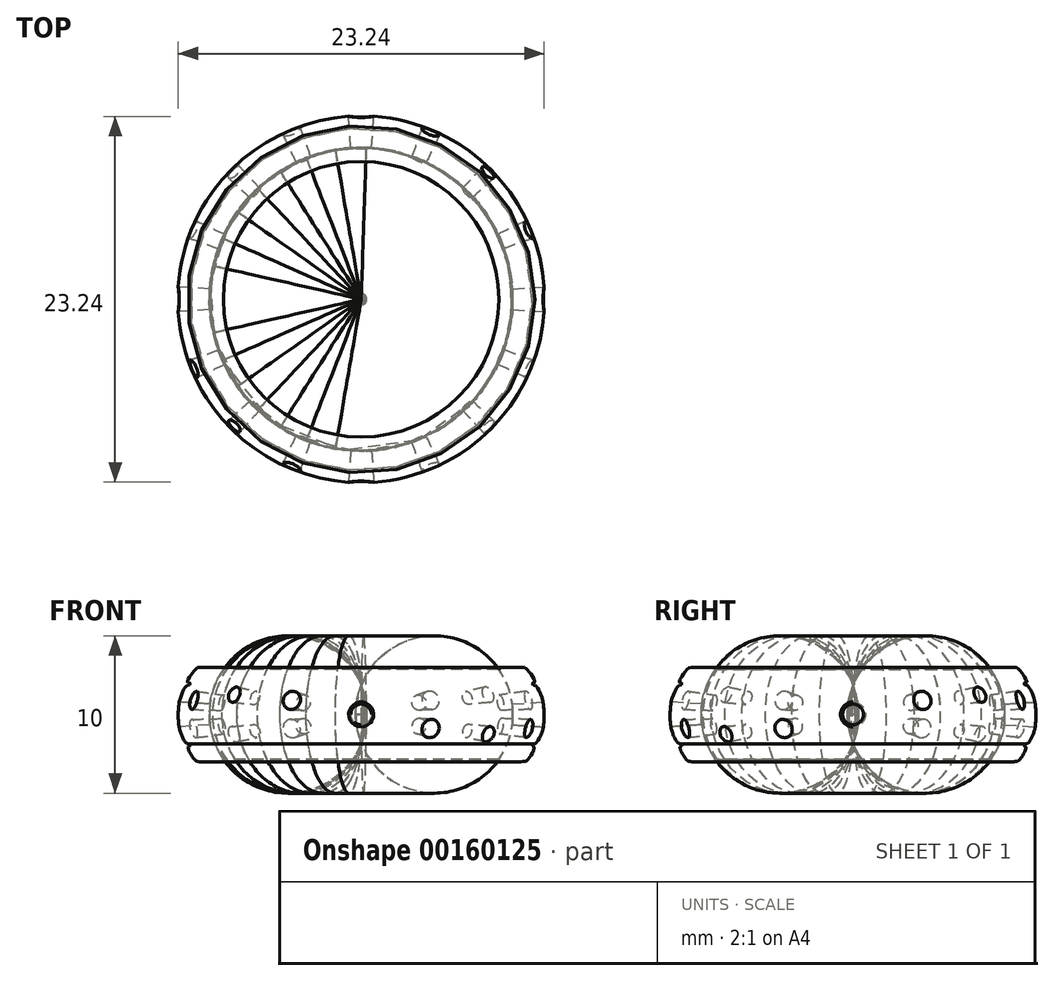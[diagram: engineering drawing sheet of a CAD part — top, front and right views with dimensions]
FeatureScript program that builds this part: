
annotation { "Feature Type Name" : "Feature", "Feature Type Description" : "" }
export const myFeature = defineFeature(function(context is Context, id is Id, definition is map)
    precondition{}
    {
        {
            var Q0;
            Q0=qCreatedBy(makeId("Top.planeOp"),FACE);
            var sketch = newSketch(context, id + "F0", { "sketchPlane" : qUnion([Q0])});
            skCircle(sketch, "E0", {"center": v(0, 0) * mm, "radius": 9.65 * mm});
            skLineSegment(sketch, "E1", {"start": v(-9.65, 0) * mm, "end": v(9.65, 0) * mm, "construction": true});
            skLineSegment(sketch, "E2", {"start": v(0, 9.65) * mm, "end": v(0, -9.65) * mm, "construction": true});
            skCircle(sketch, "E3", {"center": v(0, 0) * mm, "radius": 13.5 * mm});
            skSolve(sketch);
        }
        {
            var Q0;
            Q0=qCreatedBy(makeId("Top.planeOp"),FACE);
            var sketch = newSketch(context, id + "F1", { "sketchPlane" : qUnion([Q0])});
            skCircle(sketch, "E4.0", {"center": v(0, 0) * mm, "radius": 13.5 * mm, "construction": true});
            skLineSegment(sketch, "E5", {"start": v(0, 0) * mm, "end": v(-13.5, 0) * mm, "construction": true});
            skLineSegment(sketch, "E6", {"start": v(-13.5, 4.4) * mm, "end": v(-13.5, -4.4) * mm, "construction": true});
            skLineSegment(sketch, "E7.1.0", {"start": v(0, 0) * mm, "end": v(0, -13.5) * mm, "construction": true});
            skLineSegment(sketch, "E7.1.1", {"start": v(-4.4, -13.5) * mm, "end": v(4.4, -13.5) * mm, "construction": true});
            skLineSegment(sketch, "E7.2.0", {"start": v(0, 0) * mm, "end": v(13.5, 0) * mm, "construction": true});
            skLineSegment(sketch, "E7.2.1", {"start": v(13.5, -4.4) * mm, "end": v(13.5, 4.4) * mm, "construction": true});
            skLineSegment(sketch, "E7.3.0", {"start": v(0, 0) * mm, "end": v(0, 13.5) * mm, "construction": true});
            skLineSegment(sketch, "E7.3.1", {"start": v(4.4, 13.5) * mm, "end": v(-4.4, 13.5) * mm, "construction": true});
            skSolve(sketch);
        }
        {
            var Q0;
            Q0=qCreatedBy(makeId("Top.planeOp"),FACE);
            var sketch = newSketch(context, id + "F2", { "sketchPlane" : qUnion([Q0])});
            skCircle(sketch, "E8.0", {"center": v(0, 0) * mm, "radius": 13.5 * mm});
            skLineSegment(sketch, "E9", {"start": v(0, 0) * mm, "end": v(9.55, -9.55) * mm, "construction": true});
            skLineSegment(sketch, "E10", {"start": v(12.38, -6.71) * mm, "end": v(6.71, -12.38) * mm, "construction": true});
            skLineSegment(sketch, "E11.1.0", {"start": v(6.71, 12.38) * mm, "end": v(12.38, 6.71) * mm, "construction": true});
            skLineSegment(sketch, "E11.1.1", {"start": v(0, 0) * mm, "end": v(9.55, 9.55) * mm, "construction": true});
            skLineSegment(sketch, "E11.2.0", {"start": v(-12.38, 6.71) * mm, "end": v(-6.71, 12.38) * mm, "construction": true});
            skLineSegment(sketch, "E11.2.1", {"start": v(0, 0) * mm, "end": v(-9.55, 9.55) * mm, "construction": true});
            skLineSegment(sketch, "E11.3.0", {"start": v(-6.71, -12.38) * mm, "end": v(-12.38, -6.71) * mm, "construction": true});
            skLineSegment(sketch, "E11.3.1", {"start": v(0, 0) * mm, "end": v(-9.55, -9.55) * mm, "construction": true});
            skSolve(sketch);
        }
        {
            var Q0;
            Q0=qCreatedBy(makeId("Top.planeOp"),FACE);
            var sketch = newSketch(context, id + "F3", { "sketchPlane" : qUnion([Q0])});
            skCircle(sketch, "E12.0", {"center": v(0, 0) * mm, "radius": 13.5 * mm});
            skLineSegment(sketch, "E13", {"start": v(0, 0) * mm, "end": v(5.17, -12.47) * mm, "construction": true});
            skLineSegment(sketch, "E14", {"start": v(3.59, -13.13) * mm, "end": v(6.75, -11.82) * mm, "construction": true});
            skLineSegment(sketch, "E15.1.0", {"start": v(0, 0) * mm, "end": v(12.47, -5.17) * mm, "construction": true});
            skLineSegment(sketch, "E15.1.1", {"start": v(11.82, -6.75) * mm, "end": v(13.13, -3.59) * mm, "construction": true});
            skLineSegment(sketch, "E15.2.0", {"start": v(0, 0) * mm, "end": v(12.47, 5.17) * mm, "construction": true});
            skLineSegment(sketch, "E15.2.1", {"start": v(13.13, 3.59) * mm, "end": v(11.82, 6.75) * mm, "construction": true});
            skLineSegment(sketch, "E15.3.0", {"start": v(0, 0) * mm, "end": v(5.17, 12.47) * mm, "construction": true});
            skLineSegment(sketch, "E15.3.1", {"start": v(6.75, 11.82) * mm, "end": v(3.59, 13.13) * mm, "construction": true});
            skLineSegment(sketch, "E16.3.4.0", {"start": v(-3.59, 13.13) * mm, "end": v(-6.75, 11.82) * mm, "construction": true});
            skLineSegment(sketch, "E16.4.4.0", {"start": v(0, 0) * mm, "end": v(-5.17, 12.47) * mm, "construction": true});
            skLineSegment(sketch, "E16.3.5.0", {"start": v(-11.82, 6.75) * mm, "end": v(-13.13, 3.59) * mm, "construction": true});
            skLineSegment(sketch, "E16.4.5.0", {"start": v(0, 0) * mm, "end": v(-12.47, 5.17) * mm, "construction": true});
            skLineSegment(sketch, "E16.3.6.0", {"start": v(-13.13, -3.59) * mm, "end": v(-11.82, -6.75) * mm, "construction": true});
            skLineSegment(sketch, "E16.4.6.0", {"start": v(0, 0) * mm, "end": v(-12.47, -5.17) * mm, "construction": true});
            skLineSegment(sketch, "E16.3.7.0", {"start": v(-6.75, -11.82) * mm, "end": v(-3.59, -13.13) * mm, "construction": true});
            skLineSegment(sketch, "E16.4.7.0", {"start": v(0, 0) * mm, "end": v(-5.17, -12.47) * mm, "construction": true});
            skSolve(sketch);
        }
        {
            var Q0;
            Q0=qCreatedBy(makeId("Front.planeOp"),FACE);
            var sketch = newSketch(context, id + "F4", { "sketchPlane" : qUnion([Q0])});
            skLineSegment(sketch, "E17.0", {"start": v(-9.65, 0) * mm, "end": v(9.65, 0) * mm});
            skLineSegment(sketch, "E18", {"start": v(-9.65, 0) * mm, "end": v(-17.86, 0) * mm, "construction": true});
            skPoint(sketch, "E19", {"position": v(-9.87, 0) * mm});
            skCircle(sketch, "E20", {"center": v(-4.65, 0) * mm, "radius": 5 * mm});
            skFitSpline(sketch, "E21", {"points": [v(-9.87, 3) * mm, v(-10.53, 2.87) * mm, v(-11.03, 2.12) * mm, v(-11.01, 2.04) * mm, v(-10.9, 2.02) * mm, v(-10.9, 1.88) * mm, v(-11.05, 1.85) * mm, v(-11.65, 0) * mm, v(-11.07, -1.84) * mm, v(-10.9, -1.87) * mm, v(-10.88, -2) * mm, v(-10.99, -2.07) * mm, v(-10.61, -2.83) * mm, v(-9.87, -3) * mm], "startDerivative": vector(-13.36, 0) * mm, "endDerivative": vector(14.23, 0) * mm});
            skLineSegment(sketch, "E22", {"start": v(-9.87, 3) * mm, "end": v(-9.05, 3) * mm});
            skLineSegment(sketch, "E23", {"start": v(-8.65, 2.6) * mm, "end": v(-8.65, -2.6) * mm});
            skLineSegment(sketch, "E24", {"start": v(-9.05, -3) * mm, "end": v(-9.87, -3) * mm});
            skPoint(sketch, "E25.visualSharp", {"position": v(-8.65, 3) * mm});
            skArc(sketch, "E25.filletArc", {"start": v(-8.65, 2.6) * mm, "mid": v(-8.77, 2.88) * mm, "end": v(-9.05, 3) * mm});
            skPoint(sketch, "E26.visualSharp", {"position": v(-8.65, -3) * mm});
            skArc(sketch, "E26.filletArc", {"start": v(-9.05, -3) * mm, "mid": v(-8.77, -2.88) * mm, "end": v(-8.65, -2.6) * mm});
            skLineSegment(sketch, "E27", {"start": v(0, 17.35) * mm, "end": v(0, -28.4) * mm, "construction": true});
            skSolve(sketch);
        }
        {
            var Q0;
            Q0=sQuery(id+"F1.wireOp",EDGE,"E6");
            cPlane(context, id + "F5", {"entities" : qUnion([Q0]), "cplaneType" : CPlaneType.LINE_ANGLE, "offset" : 25 * mm, "angle" : 90 * degree, "width" : 150 * mm, "height" : 150 * mm});
        }
        {
            var Q0;
            Q0=qCreatedBy(id+"F5.planeOp",FACE);
            var sketch = newSketch(context, id + "F6", { "sketchPlane" : qUnion([Q0])});
            skLineSegment(sketch, "E28", {"start": v(0, 2.8) * mm, "end": v(0, -2.73) * mm, "construction": true});
            skCircle(sketch, "E29", {"center": v(0, 0) * mm, "radius": 0.93 * mm});
            skSolve(sketch);
        }
        {
            var Q0;
            Q0=makeQuery(id+"F4.imprint","IMPRINT",FACE,{"disambiguationData":[TD([[makeQuery(id+"F4.imprint","IMPRINT",EDGE,{"derivedFrom":sQuery(id+"F4.wireOp",EDGE,"E21")}),1.0]])]});
            var Q1;
            Q1=sQuery(id+"F4.wireOp",EDGE,"E27");
            revolve(context, id + "F7", {"entities" : qUnion([Q0]), "axis" : qUnion([Q1]), "revolveType" : RevolveType.FULL});
        }
        {
            var Q0;
            Q0=makeQuery(id+"F6.imprint","IMPRINT",FACE,{"disambiguationData":[TD([[makeQuery(id+"F6.imprint","IMPRINT",EDGE,{"derivedFrom":sQuery(id+"F6.wireOp",EDGE,"E29")}),1.0]])]});
            var Q1;
            Q1=sQuery(id+"F1.wireOp",VERTEX,"E4.0.center");
            loft(context, id + "F8", {"operationType" : NewBodyOperationType.REMOVE, "sheetProfilesArray" : [{ "sheetProfileEntities" : qUnion([Q0]) }, { "sheetProfileEntities" : qUnion([Q1]) }]});
        }
        {
            var Q0;
            Q0=sQuery(id+"F1.wireOp",EDGE,"E7.3.1");
            cPlane(context, id + "F9", {"entities" : qUnion([Q0]), "cplaneType" : CPlaneType.LINE_ANGLE, "offset" : 25 * mm, "angle" : 0 * degree, "width" : 150 * mm, "height" : 150 * mm});
        }
        {
            var Q0;
            Q0=qCreatedBy(id+"F9.planeOp",FACE);
            var sketch = newSketch(context, id + "F10", { "sketchPlane" : qUnion([Q0])});
            skCircle(sketch, "E30", {"center": v(0, 0) * mm, "radius": 0.93 * mm});
            skSolve(sketch);
        }
        {
            var Q1;
            Q1=makeQuery(id+"F10.imprint","IMPRINT",FACE,{"disambiguationData":[TD([[makeQuery(id+"F10.imprint","IMPRINT",EDGE,{"derivedFrom":sQuery(id+"F10.wireOp",EDGE,"E30")}),1.0]])]});
            var Q2;
            Q2=sQuery(id+"F1.wireOp",VERTEX,"E4.0.center");
            loft(context, id + "F11", {"operationType" : NewBodyOperationType.REMOVE, "sheetProfilesArray" : [{ "sheetProfileEntities" : qUnion([Q1]) }, { "sheetProfileEntities" : qUnion([Q2]) }]});
        }
        {
            var Q0;
            Q0=sQuery(id+"F1.wireOp",EDGE,"E7.2.1");
            cPlane(context, id + "F12", {"entities" : qUnion([Q0]), "cplaneType" : CPlaneType.LINE_ANGLE, "offset" : 25 * mm, "angle" : 90 * degree, "width" : 150 * mm, "height" : 150 * mm});
        }
        {
            var Q0;
            Q0=qCreatedBy(id+"F12.planeOp",FACE);
            var sketch = newSketch(context, id + "F13", { "sketchPlane" : qUnion([Q0])});
            skCircle(sketch, "E31", {"center": v(0, 0) * mm, "radius": 0.93 * mm});
            skSolve(sketch);
        }
        {
            var Q1;
            Q1=makeQuery(id+"F13.imprint","IMPRINT",FACE,{"disambiguationData":[TD([[makeQuery(id+"F13.imprint","IMPRINT",EDGE,{"derivedFrom":sQuery(id+"F13.wireOp",EDGE,"E31")}),1.0]])]});
            var Q2;
            Q2=sQuery(id+"F1.wireOp",VERTEX,"E4.0.center");
            loft(context, id + "F14", {"operationType" : NewBodyOperationType.REMOVE, "sheetProfilesArray" : [{ "sheetProfileEntities" : qUnion([Q1]) }, { "sheetProfileEntities" : qUnion([Q2]) }]});
        }
        {
            var Q0;
            Q0=sQuery(id+"F1.wireOp",EDGE,"E7.1.1");
            cPlane(context, id + "F15", {"entities" : qUnion([Q0]), "cplaneType" : CPlaneType.LINE_ANGLE, "offset" : 25 * mm, "angle" : 0 * degree, "width" : 150 * mm, "height" : 150 * mm});
        }
        {
            var Q0;
            Q0=qCreatedBy(id+"F15.planeOp",FACE);
            var sketch = newSketch(context, id + "F16", { "sketchPlane" : qUnion([Q0])});
            skCircle(sketch, "E32", {"center": v(0, 0) * mm, "radius": 0.93 * mm});
            skSolve(sketch);
        }
        {
            var Q1;
            Q1=makeQuery(id+"F16.imprint","IMPRINT",FACE,{"disambiguationData":[TD([[makeQuery(id+"F16.imprint","IMPRINT",EDGE,{"derivedFrom":sQuery(id+"F16.wireOp",EDGE,"E32")}),1.0]])]});
            var Q2;
            Q2=sQuery(id+"F1.wireOp",VERTEX,"E4.0.center");
            loft(context, id + "F17", {"operationType" : NewBodyOperationType.REMOVE, "sheetProfilesArray" : [{ "sheetProfileEntities" : qUnion([Q1]) }, { "sheetProfileEntities" : qUnion([Q2]) }]});
        }
        {
            var Q0;
            Q0=sQuery(id+"F2.wireOp",EDGE,"E10");
            cPlane(context, id + "F18", {"entities" : qUnion([Q0]), "cplaneType" : CPlaneType.LINE_ANGLE, "offset" : 25 * mm, "angle" : 90 * degree, "width" : 150 * mm, "height" : 150 * mm});
        }
        {
            var Q0;
            Q0=qCreatedBy(id+"F18.planeOp",FACE);
            var sketch = newSketch(context, id + "F19", { "sketchPlane" : qUnion([Q0])});
            skLineSegment(sketch, "E33", {"start": v(0, 0) * mm, "end": v(0, -6.97) * mm, "construction": true});
            skCircle(sketch, "E34", {"center": v(0, -1.5) * mm, "radius": 0.6 * mm});
            skSolve(sketch);
        }
        {
            var Q1;
            Q1=makeQuery(id+"F19.imprint","IMPRINT",FACE,{"disambiguationData":[TD([[makeQuery(id+"F19.imprint","IMPRINT",EDGE,{"derivedFrom":sQuery(id+"F19.wireOp",EDGE,"E34")}),1.0]])]});
            var Q2;
            Q2=sQuery(id+"F1.wireOp",VERTEX,"E4.0.center");
            loft(context, id + "F20", {"operationType" : NewBodyOperationType.REMOVE, "sheetProfilesArray" : [{ "sheetProfileEntities" : qUnion([Q1]) }, { "sheetProfileEntities" : qUnion([Q2]) }]});
        }
        {
            var Q0;
            Q0=sQuery(id+"F2.wireOp",EDGE,"E11.3.0");
            cPlane(context, id + "F21", {"entities" : qUnion([Q0]), "cplaneType" : CPlaneType.LINE_ANGLE, "offset" : 25 * mm, "angle" : 90 * degree, "width" : 150 * mm, "height" : 150 * mm});
        }
        {
            var Q0;
            Q0=qCreatedBy(id+"F21.planeOp",FACE);
            var sketch = newSketch(context, id + "F22", { "sketchPlane" : qUnion([Q0])});
            skLineSegment(sketch, "E35", {"start": v(0, -4.31) * mm, "end": v(0, 5.75) * mm, "construction": true});
            skCircle(sketch, "E36", {"center": v(0, 1.5) * mm, "radius": 0.6 * mm});
            skSolve(sketch);
        }
        {
            var Q1;
            Q1=makeQuery(id+"F22.imprint","IMPRINT",FACE,{"disambiguationData":[TD([[makeQuery(id+"F22.imprint","IMPRINT",EDGE,{"derivedFrom":sQuery(id+"F22.wireOp",EDGE,"E36")}),1.0]])]});
            var Q2;
            Q2=sQuery(id+"F1.wireOp",VERTEX,"E4.0.center");
            loft(context, id + "F23", {"operationType" : NewBodyOperationType.REMOVE, "sheetProfilesArray" : [{ "sheetProfileEntities" : qUnion([Q1]) }, { "sheetProfileEntities" : qUnion([Q2]) }]});
        }
        {
            var Q0;
            Q0=sQuery(id+"F2.wireOp",EDGE,"E11.2.0");
            cPlane(context, id + "F24", {"entities" : qUnion([Q0]), "cplaneType" : CPlaneType.LINE_ANGLE, "offset" : 25 * mm, "angle" : 90 * degree, "width" : 150 * mm, "height" : 150 * mm});
        }
        {
            var Q0;
            Q0=qCreatedBy(id+"F24.planeOp",FACE);
            var sketch = newSketch(context, id + "F25", { "sketchPlane" : qUnion([Q0])});
            skLineSegment(sketch, "E37", {"start": v(0, 5.18) * mm, "end": v(0, -5.52) * mm, "construction": true});
            skCircle(sketch, "E38", {"center": v(0, -1.5) * mm, "radius": 0.6 * mm});
            skSolve(sketch);
        }
        {
            var Q1;
            Q1=makeQuery(id+"F25.imprint","IMPRINT",FACE,{"disambiguationData":[TD([[makeQuery(id+"F25.imprint","IMPRINT",EDGE,{"derivedFrom":sQuery(id+"F25.wireOp",EDGE,"E38")}),1.0]])]});
            var Q2;
            Q2=sQuery(id+"F1.wireOp",VERTEX,"E4.0.center");
            loft(context, id + "F26", {"operationType" : NewBodyOperationType.REMOVE, "sheetProfilesArray" : [{ "sheetProfileEntities" : qUnion([Q1]) }, { "sheetProfileEntities" : qUnion([Q2]) }]});
        }
        {
            var Q0;
            Q0=sQuery(id+"F2.wireOp",EDGE,"E11.1.0");
            cPlane(context, id + "F27", {"entities" : qUnion([Q0]), "cplaneType" : CPlaneType.LINE_ANGLE, "offset" : 25 * mm, "angle" : 90 * degree, "width" : 150 * mm, "height" : 150 * mm});
        }
        {
            var Q0;
            Q0=qCreatedBy(id+"F27.planeOp",FACE);
            var sketch = newSketch(context, id + "F28", { "sketchPlane" : qUnion([Q0])});
            skLineSegment(sketch, "E39", {"start": v(0, -3.41) * mm, "end": v(0, 4.01) * mm, "construction": true});
            skCircle(sketch, "E40", {"center": v(0, 1.5) * mm, "radius": 0.6 * mm});
            skSolve(sketch);
        }
        {
            var Q1;
            Q1=makeQuery(id+"F28.imprint","IMPRINT",FACE,{"disambiguationData":[TD([[makeQuery(id+"F28.imprint","IMPRINT",EDGE,{"derivedFrom":sQuery(id+"F28.wireOp",EDGE,"E40")}),1.0]])]});
            var Q2;
            Q2=sQuery(id+"F1.wireOp",VERTEX,"E4.0.center");
            loft(context, id + "F29", {"operationType" : NewBodyOperationType.REMOVE, "sheetProfilesArray" : [{ "sheetProfileEntities" : qUnion([Q1]) }, { "sheetProfileEntities" : qUnion([Q2]) }]});
        }
        {
            var Q0;
            Q0=sQuery(id+"F3.wireOp",EDGE,"E14");
            cPlane(context, id + "F30", {"entities" : qUnion([Q0]), "cplaneType" : CPlaneType.LINE_ANGLE, "offset" : 25 * mm, "angle" : 0 * degree, "width" : 150 * mm, "height" : 150 * mm});
        }
        {
            var Q0;
            Q0=qCreatedBy(id+"F30.planeOp",FACE);
            var sketch = newSketch(context, id + "F31", { "sketchPlane" : qUnion([Q0])});
            skLineSegment(sketch, "E41", {"start": v(0, 1.86) * mm, "end": v(0, -3.93) * mm, "construction": true});
            skCircle(sketch, "E42", {"center": v(0, -1.06) * mm, "radius": 0.7 * mm});
            skSolve(sketch);
        }
        {
            var Q1;
            Q1=makeQuery(id+"F31.imprint","IMPRINT",FACE,{"disambiguationData":[TD([[makeQuery(id+"F31.imprint","IMPRINT",EDGE,{"derivedFrom":sQuery(id+"F31.wireOp",EDGE,"E42")}),1.0]])]});
            var Q2;
            Q2=sQuery(id+"F3.wireOp",VERTEX,"E12.0.center");
            loft(context, id + "F32", {"operationType" : NewBodyOperationType.REMOVE, "sheetProfilesArray" : [{ "sheetProfileEntities" : qUnion([Q1]) }, { "sheetProfileEntities" : qUnion([Q2]) }]});
        }
        {
            var Q0;
            Q0=sQuery(id+"F3.wireOp",EDGE,"E16.3.7.0");
            cPlane(context, id + "F33", {"entities" : qUnion([Q0]), "cplaneType" : CPlaneType.LINE_ANGLE, "offset" : 25 * mm, "angle" : 0 * degree, "width" : 150 * mm, "height" : 150 * mm});
        }
        {
            var Q0;
            Q0=qCreatedBy(id+"F33.planeOp",FACE);
            var sketch = newSketch(context, id + "F34", { "sketchPlane" : qUnion([Q0])});
            skLineSegment(sketch, "E43", {"start": v(0, -5.3) * mm, "end": v(0, 5.97) * mm, "construction": true});
            skCircle(sketch, "E44", {"center": v(0, 1.06) * mm, "radius": 0.7 * mm});
            skSolve(sketch);
        }
        {
            var Q1;
            Q1=makeQuery(id+"F34.imprint","IMPRINT",FACE,{"disambiguationData":[TD([[makeQuery(id+"F34.imprint","IMPRINT",EDGE,{"derivedFrom":sQuery(id+"F34.wireOp",EDGE,"E44")}),1.0]])]});
            var Q2;
            Q2=sQuery(id+"F3.wireOp",VERTEX,"E12.0.center");
            loft(context, id + "F35", {"operationType" : NewBodyOperationType.REMOVE, "sheetProfilesArray" : [{ "sheetProfileEntities" : qUnion([Q1]) }, { "sheetProfileEntities" : qUnion([Q2]) }]});
        }
        {
            var Q0;
            Q0=sQuery(id+"F3.wireOp",EDGE,"E16.3.6.0");
            cPlane(context, id + "F36", {"entities" : qUnion([Q0]), "cplaneType" : CPlaneType.LINE_ANGLE, "offset" : 25 * mm, "angle" : 90 * degree, "width" : 150 * mm, "height" : 150 * mm});
        }
        {
            var Q0;
            Q0=qCreatedBy(id+"F36.planeOp",FACE);
            var sketch = newSketch(context, id + "F37", { "sketchPlane" : qUnion([Q0])});
            skLineSegment(sketch, "E45", {"start": v(0, -0.9) * mm, "end": v(0, 3) * mm, "construction": true});
            skCircle(sketch, "E46", {"center": v(0, 1.06) * mm, "radius": 0.7 * mm});
            skSolve(sketch);
        }
        {
            var Q1;
            Q1=makeQuery(id+"F37.imprint","IMPRINT",FACE,{"disambiguationData":[TD([[makeQuery(id+"F37.imprint","IMPRINT",EDGE,{"derivedFrom":sQuery(id+"F37.wireOp",EDGE,"E46")}),1.0]])]});
            var Q2;
            Q2=sQuery(id+"F3.wireOp",VERTEX,"E12.0.center");
            loft(context, id + "F38", {"operationType" : NewBodyOperationType.REMOVE, "sheetProfilesArray" : [{ "sheetProfileEntities" : qUnion([Q1]) }, { "sheetProfileEntities" : qUnion([Q2]) }]});
        }
        {
            var Q0;
            Q0=sQuery(id+"F3.wireOp",EDGE,"E16.3.5.0");
            cPlane(context, id + "F39", {"entities" : qUnion([Q0]), "cplaneType" : CPlaneType.LINE_ANGLE, "offset" : 25 * mm, "angle" : 90 * degree, "width" : 150 * mm, "height" : 150 * mm});
        }
        {
            var Q0;
            Q0=qCreatedBy(id+"F39.planeOp",FACE);
            var sketch = newSketch(context, id + "F40", { "sketchPlane" : qUnion([Q0])});
            skLineSegment(sketch, "E47", {"start": v(0, 0) * mm, "end": v(0, -2.12) * mm, "construction": true});
            skCircle(sketch, "E48", {"center": v(0, -1.06) * mm, "radius": 0.7 * mm});
            skSolve(sketch);
        }
        {
            var Q1;
            Q1=makeQuery(id+"F40.imprint","IMPRINT",FACE,{"disambiguationData":[TD([[makeQuery(id+"F40.imprint","IMPRINT",EDGE,{"derivedFrom":sQuery(id+"F40.wireOp",EDGE,"E48")}),1.0]])]});
            var Q2;
            Q2=sQuery(id+"F3.wireOp",VERTEX,"E12.0.center");
            loft(context, id + "F41", {"operationType" : NewBodyOperationType.REMOVE, "sheetProfilesArray" : [{ "sheetProfileEntities" : qUnion([Q1]) }, { "sheetProfileEntities" : qUnion([Q2]) }]});
        }
        {
            var Q0;
            Q0=sQuery(id+"F3.wireOp",EDGE,"E16.3.4.0");
            cPlane(context, id + "F42", {"entities" : qUnion([Q0]), "cplaneType" : CPlaneType.LINE_ANGLE, "offset" : 25 * mm, "angle" : 0 * degree, "width" : 150 * mm, "height" : 150 * mm});
        }
        {
            var Q0;
            Q0=qCreatedBy(id+"F42.planeOp",FACE);
            var sketch = newSketch(context, id + "F43", { "sketchPlane" : qUnion([Q0])});
            skLineSegment(sketch, "E49", {"start": v(0, 0) * mm, "end": v(0, -3.77) * mm, "construction": true});
            skCircle(sketch, "E50", {"center": v(0, -1.06) * mm, "radius": 0.7 * mm});
            skSolve(sketch);
        }
        {
            var Q1;
            Q1=sQuery(id+"F3.wireOp",VERTEX,"E12.0.center");
            var Q2;
            Q2=makeQuery(id+"F43.imprint","IMPRINT",FACE,{"disambiguationData":[TD([[makeQuery(id+"F43.imprint","IMPRINT",EDGE,{"derivedFrom":sQuery(id+"F43.wireOp",EDGE,"E50")}),1.0]])]});
            loft(context, id + "F44", {"operationType" : NewBodyOperationType.REMOVE, "sheetProfilesArray" : [{ "sheetProfileEntities" : qUnion([Q1]) }, { "sheetProfileEntities" : qUnion([Q2]) }]});
        }
        {
            var Q0;
            Q0=sQuery(id+"F3.wireOp",EDGE,"E15.3.1");
            cPlane(context, id + "F45", {"entities" : qUnion([Q0]), "cplaneType" : CPlaneType.LINE_ANGLE, "offset" : 25 * mm, "angle" : 0 * degree, "width" : 150 * mm, "height" : 150 * mm});
        }
        {
            var Q0;
            Q0=qCreatedBy(id+"F45.planeOp",FACE);
            var sketch = newSketch(context, id + "F46", { "sketchPlane" : qUnion([Q0])});
            skLineSegment(sketch, "E51", {"start": v(0, 0) * mm, "end": v(0, 2.17) * mm, "construction": true});
            skCircle(sketch, "E52", {"center": v(0, 1.06) * mm, "radius": 0.7 * mm});
            skSolve(sketch);
        }
        {
            var Q1;
            Q1=makeQuery(id+"F46.imprint","IMPRINT",FACE,{"disambiguationData":[TD([[makeQuery(id+"F46.imprint","IMPRINT",EDGE,{"derivedFrom":sQuery(id+"F46.wireOp",EDGE,"E52")}),1.0]])]});
            var Q2;
            Q2=sQuery(id+"F3.wireOp",VERTEX,"E12.0.center");
            loft(context, id + "F47", {"operationType" : NewBodyOperationType.REMOVE, "sheetProfilesArray" : [{ "sheetProfileEntities" : qUnion([Q1]) }, { "sheetProfileEntities" : qUnion([Q2]) }]});
        }
        {
            var Q0;
            Q0=sQuery(id+"F3.wireOp",EDGE,"E15.2.1");
            cPlane(context, id + "F48", {"entities" : qUnion([Q0]), "cplaneType" : CPlaneType.LINE_ANGLE, "offset" : 25 * mm, "angle" : 90 * degree, "width" : 150 * mm, "height" : 150 * mm});
        }
        {
            var Q0;
            Q0=qCreatedBy(id+"F48.planeOp",FACE);
            var sketch = newSketch(context, id + "F49", { "sketchPlane" : qUnion([Q0])});
            skLineSegment(sketch, "E53", {"start": v(0, 0) * mm, "end": v(0, 3.06) * mm, "construction": true});
            skCircle(sketch, "E54", {"center": v(0, 1.06) * mm, "radius": 0.7 * mm});
            skSolve(sketch);
        }
        {
            var Q1;
            Q1=makeQuery(id+"F49.imprint","IMPRINT",FACE,{"disambiguationData":[TD([[makeQuery(id+"F49.imprint","IMPRINT",EDGE,{"derivedFrom":sQuery(id+"F49.wireOp",EDGE,"E54")}),1.0]])]});
            var Q2;
            Q2=sQuery(id+"F3.wireOp",VERTEX,"E12.0.center");
            loft(context, id + "F50", {"operationType" : NewBodyOperationType.REMOVE, "sheetProfilesArray" : [{ "sheetProfileEntities" : qUnion([Q1]) }, { "sheetProfileEntities" : qUnion([Q2]) }]});
        }
        {
            var Q0;
            Q0=sQuery(id+"F3.wireOp",EDGE,"E15.1.1");
            cPlane(context, id + "F51", {"entities" : qUnion([Q0]), "cplaneType" : CPlaneType.LINE_ANGLE, "offset" : 25 * mm, "angle" : 90 * degree, "width" : 150 * mm, "height" : 150 * mm});
        }
        {
            var Q0;
            Q0=qCreatedBy(id+"F51.planeOp",FACE);
            var sketch = newSketch(context, id + "F52", { "sketchPlane" : qUnion([Q0])});
            skLineSegment(sketch, "E55", {"start": v(0, 0) * mm, "end": v(0, -1.7) * mm, "construction": true});
            skCircle(sketch, "E56", {"center": v(0, -1.06) * mm, "radius": 0.7 * mm});
            skSolve(sketch);
        }
        {
            var Q1;
            Q1=makeQuery(id+"F52.imprint","IMPRINT",FACE,{"disambiguationData":[TD([[makeQuery(id+"F52.imprint","IMPRINT",EDGE,{"derivedFrom":sQuery(id+"F52.wireOp",EDGE,"E56")}),1.0]])]});
            var Q2;
            Q2=sQuery(id+"F3.wireOp",VERTEX,"E12.0.center");
            loft(context, id + "F53", {"operationType" : NewBodyOperationType.REMOVE, "sheetProfilesArray" : [{ "sheetProfileEntities" : qUnion([Q1]) }, { "sheetProfileEntities" : qUnion([Q2]) }]});
        }
    });
